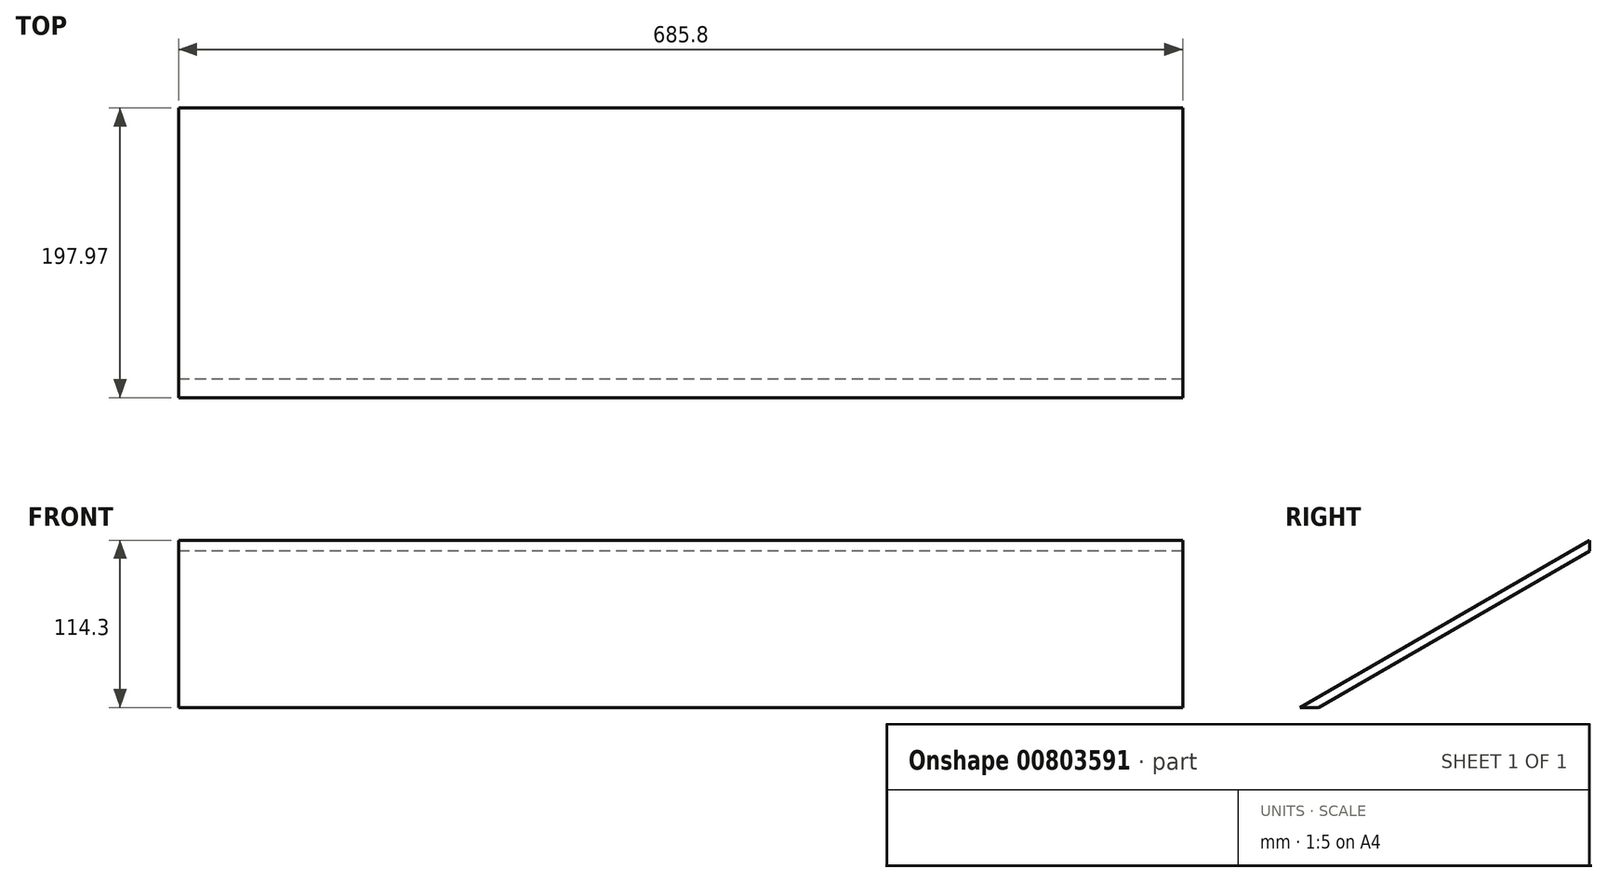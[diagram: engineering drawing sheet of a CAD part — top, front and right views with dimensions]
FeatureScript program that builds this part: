
annotation { "Feature Type Name" : "Feature", "Feature Type Description" : "" }
export const myFeature = defineFeature(function(context is Context, id is Id, definition is map)
    precondition{}
    {
        {
            var Q0;
            Q0=qCreatedBy(makeId("Right.planeOp"),FACE);
            var sketch = newSketch(context, id + "F0", { "sketchPlane" : qUnion([Q0])});
            skLineSegment(sketch, "E0", {"start": v(-197.97, 0) * mm, "end": v(0, 114.3) * mm});
            skLineSegment(sketch, "E1", {"start": v(-197.97, 0) * mm, "end": v(-185.27, 0) * mm});
            skLineSegment(sketch, "E2", {"start": v(-185.27, 0) * mm, "end": v(0, 106.97) * mm});
            skLineSegment(sketch, "E3", {"start": v(0, 106.97) * mm, "end": v(0, 114.3) * mm});
            skSolve(sketch);
        }
        {
            var Q0;
            Q0 = qSketchRegion(id + "F0", true);
            extrude(context, id + "F1", {"entities" : qUnion([Q0]), "endBound" : BoundingType.SYMMETRIC, "depth" : 685.8 * mm, "offsetDistance" : 25.4 * mm});
        }
    });
